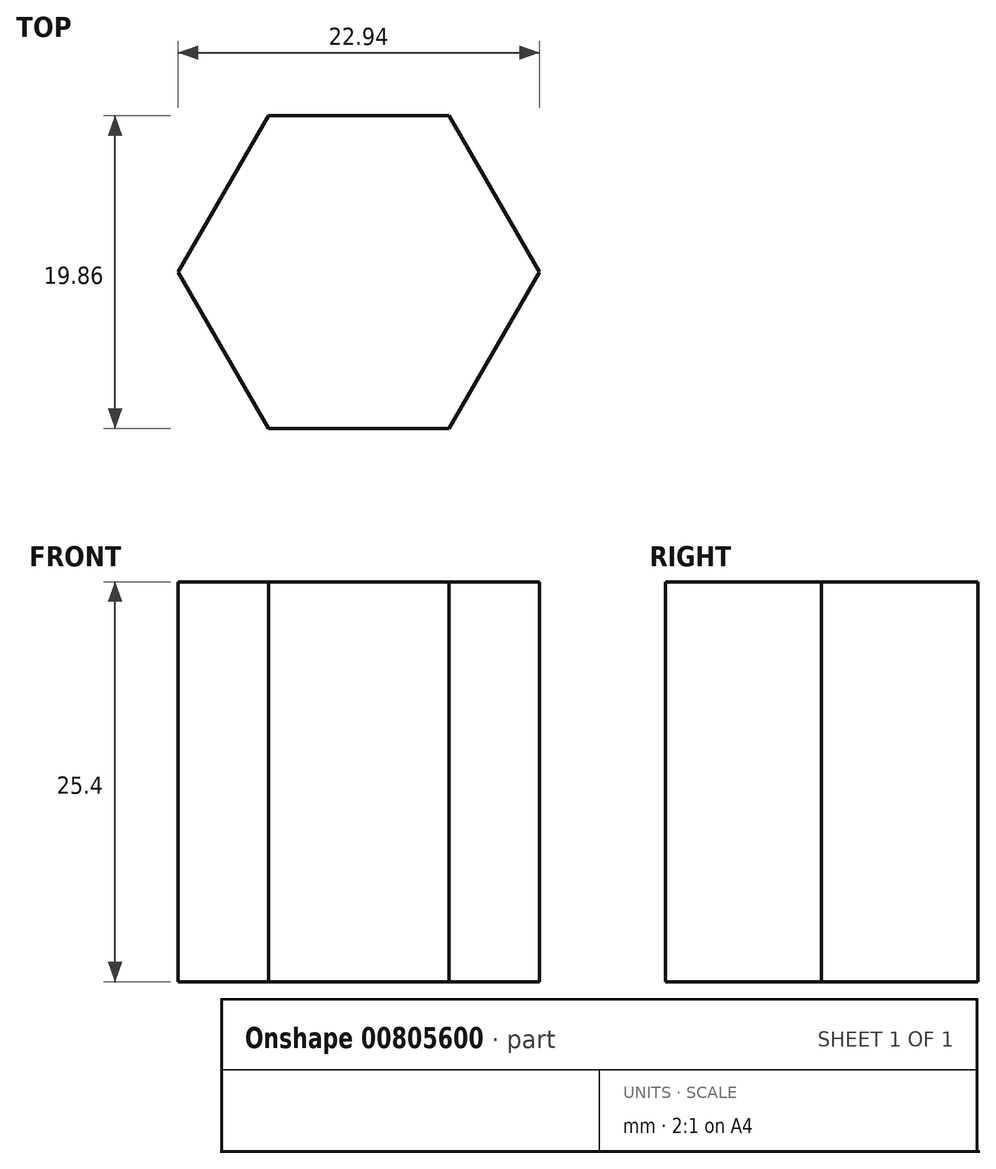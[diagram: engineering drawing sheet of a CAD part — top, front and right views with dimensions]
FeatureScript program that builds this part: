
annotation { "Feature Type Name" : "Feature", "Feature Type Description" : "" }
export const myFeature = defineFeature(function(context is Context, id is Id, definition is map)
    precondition{}
    {
        {
            var Q0;
            Q0=qCreatedBy(makeId("Top.planeOp"),FACE);
            var sketch = newSketch(context, id + "F0", { "sketchPlane" : qUnion([Q0])});
            skCircle(sketch, "E0.cCircle", {"center": v(0, 0) * mm, "radius": 9.93 * mm, "construction": true});
            skLineSegment(sketch, "E0.0", {"start": v(-5.73, 9.93) * mm, "end": v(5.73, 9.93) * mm});
            skLineSegment(sketch, "E0.1", {"start": v(5.73, 9.93) * mm, "end": v(11.47, 0) * mm});
            skLineSegment(sketch, "E0.2", {"start": v(11.47, 0) * mm, "end": v(5.73, -9.93) * mm});
            skLineSegment(sketch, "E0.3", {"start": v(5.73, -9.93) * mm, "end": v(-5.73, -9.93) * mm});
            skLineSegment(sketch, "E0.4", {"start": v(-5.73, -9.93) * mm, "end": v(-11.47, 0) * mm});
            skLineSegment(sketch, "E0.5", {"start": v(-11.47, 0) * mm, "end": v(-5.73, 9.93) * mm});
            skPoint(sketch, "E0.0.midPoint", {"position": v(0, 9.93) * mm});
            skSolve(sketch);
        }
        {
            var Q0;
            Q0 = qSketchRegion(id + "F0", true);
            extrude(context, id + "F1", {"entities" : qUnion([Q0]), "depth" : 25.4 * mm, "offsetDistance" : 25.4 * mm});
        }
    });
